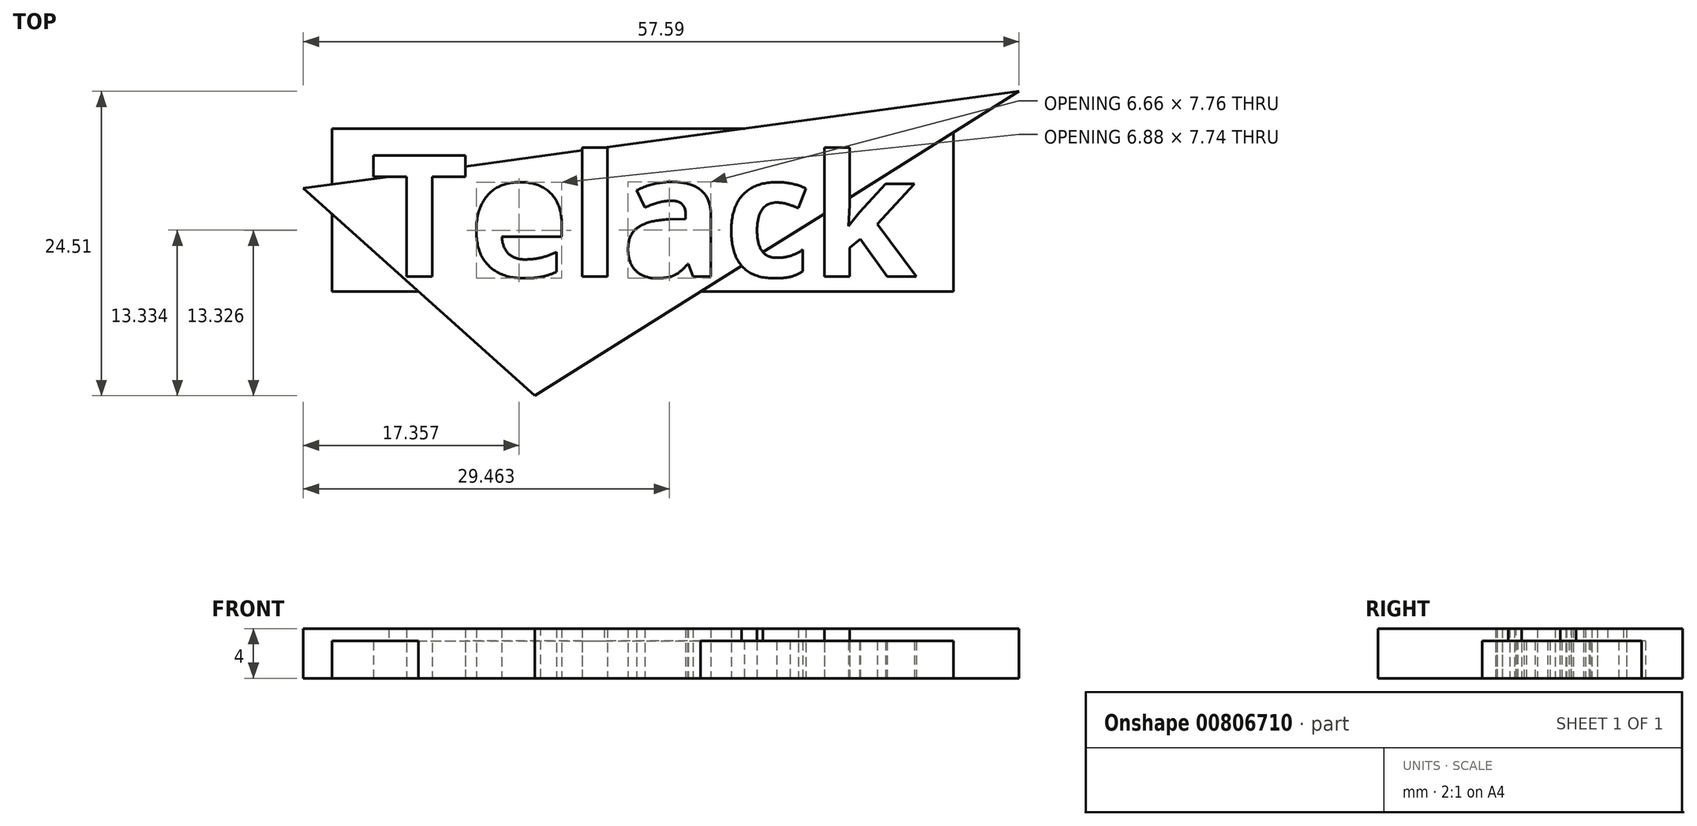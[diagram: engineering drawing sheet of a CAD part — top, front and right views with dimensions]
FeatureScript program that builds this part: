
annotation { "Feature Type Name" : "Feature", "Feature Type Description" : "" }
export const myFeature = defineFeature(function(context is Context, id is Id, definition is map)
    precondition{}
    {
        {
            var Q0;
            Q0=qCreatedBy(makeId("Top.planeOp"),FACE);
            var sketch = newSketch(context, id + "F0", { "sketchPlane" : qUnion([Q0])});
            skLineSegment(sketch, "E0.bottom", {"start": v(-26.01, 30.37) * mm, "end": v(23.99, 30.37) * mm});
            skLineSegment(sketch, "E0.top", {"start": v(-26.01, 17.25) * mm, "end": v(23.99, 17.25) * mm});
            skLineSegment(sketch, "E0.left", {"start": v(-26.01, 30.37) * mm, "end": v(-26.01, 17.25) * mm});
            skLineSegment(sketch, "E0.right", {"start": v(23.99, 30.37) * mm, "end": v(23.99, 17.25) * mm});
            skLineSegment(sketch, "E1", {"start": v(-28.33, 25.56) * mm, "end": v(29.26, 33.37) * mm});
            skLineSegment(sketch, "E2", {"start": v(29.26, 33.37) * mm, "end": v(-9.7, 8.86) * mm});
            skLineSegment(sketch, "E3", {"start": v(-9.7, 8.86) * mm, "end": v(-28.33, 25.56) * mm});
            skText(sketch, "E4", { "text": "Telack", "fontName": "OpenSans-Bold.ttf"});
            const initialGuessF0  = {"E4": [-0.02295, 0.01845, 1, 0, 0.00985]};
            skSetInitialGuess(sketch, initialGuessF0);
            skSolve(sketch);
        }
        {
            var Q0;
            Q0=makeQuery(id+"F0.imprint","IMPRINT",FACE,{"disambiguationData":[TD([[makeQuery(id+"F0.imprint","IMPRINT",EDGE,{"derivedFrom":sQuery(id+"F0.wireOp",EDGE,"E4.sketch_text.stroke-0")}),1.0]])]});
            var Q1;
            {var subQ1=sQuery(id+"F0.wireOp",EDGE,"E4.sketch_text.stroke-3");Q1=makeQuery(id+"F0.imprint","IMPRINT",FACE,{"disambiguationData":[TD([[makeQuery(id+"F0.imprint","IMPRINT",EDGE,{"derivedFrom":subQ1}),1.0]])]});}
            var Q2;
            {var subQ14=sQuery(id+"F0.wireOp",EDGE,"E4.sketch_text.stroke-66");Q2=makeQuery(id+"F0.imprint","IMPRINT",FACE,{"disambiguationData":[TD([[makeQuery(id+"F0.imprint","IMPRINT",EDGE,{"derivedFrom":subQ14}),1.0]])]});}
            var Q3;
            {var subQ0=sQuery(id+"F0.wireOp",EDGE,"E0.left");var subQ1=sQuery(id+"F0.wireOp",EDGE,"E0.top");var subQ2=makeQuery(id+"F0.imprint","INTERSECT",VERTEX,{"derivedFrom":[subQ1,subQ0]});Q3=makeQuery(id+"F0.imprint","IMPRINT",FACE,{"disambiguationData":[TD([[makeQuery(id+"F0.imprint","IMPRINT",EDGE,{"disambiguationData":[TD([[subQ2,-1.0]])],"derivedFrom":subQ1}),1.0]])]});}
            extrude(context, id + "F1", {"entities" : qUnion([Q0, Q1, Q2, Q3]), "depth" : 3 * mm, "offsetDistance" : 25 * mm});
        }
        {
            var Q0;
            Q0=makeQuery(id+"F0.imprint","IMPRINT",FACE,{"disambiguationData":[TD([[makeQuery(id+"F0.imprint","IMPRINT",EDGE,{"derivedFrom":sQuery(id+"F0.wireOp",EDGE,"E4.sketch_text.stroke-0")}),1.0]])]});
            var Q1;
            {var subQ0=sQuery(id+"F0.wireOp",EDGE,"E1");var subQ1=sQuery(id+"F0.wireOp",EDGE,"E0.left");var subQ2=makeQuery(id+"F0.imprint","INTERSECT",VERTEX,{"derivedFrom":[subQ1,subQ0]});Q1=makeQuery(id+"F0.imprint","IMPRINT",FACE,{"disambiguationData":[TD([[makeQuery(id+"F0.imprint","IMPRINT",EDGE,{"disambiguationData":[TD([[subQ2,-1.0]])],"derivedFrom":subQ1}),-1.0]])]});}
            var Q2;
            {var subQ0=sQuery(id+"F0.wireOp",EDGE,"E3");var subQ1=sQuery(id+"F0.wireOp",EDGE,"E0.top");var subQ2=makeQuery(id+"F0.imprint","INTERSECT",VERTEX,{"derivedFrom":[subQ1,subQ0]});Q2=makeQuery(id+"F0.imprint","IMPRINT",FACE,{"disambiguationData":[TD([[makeQuery(id+"F0.imprint","IMPRINT",EDGE,{"disambiguationData":[TD([[subQ2,-1.0]])],"derivedFrom":subQ1}),-1.0]])]});}
            var Q3;
            {var subQ0=sQuery(id+"F0.wireOp",EDGE,"E0.right");var subQ1=sQuery(id+"F0.wireOp",EDGE,"E0.bottom");var subQ2=makeQuery(id+"F0.imprint","INTERSECT",VERTEX,{"derivedFrom":[subQ1,subQ0]});Q3=makeQuery(id+"F0.imprint","IMPRINT",FACE,{"disambiguationData":[TD([[makeQuery(id+"F0.imprint","IMPRINT",EDGE,{"disambiguationData":[TD([[subQ2,1.0]])],"derivedFrom":subQ1}),1.0]])]});}
            extrude(context, id + "F2", {"entities" : qUnion([Q0, Q1, Q2, Q3]), "operationType" : NewBodyOperationType.ADD, "depth" : 4 * mm, "offsetDistance" : 25 * mm});
        }
    });
